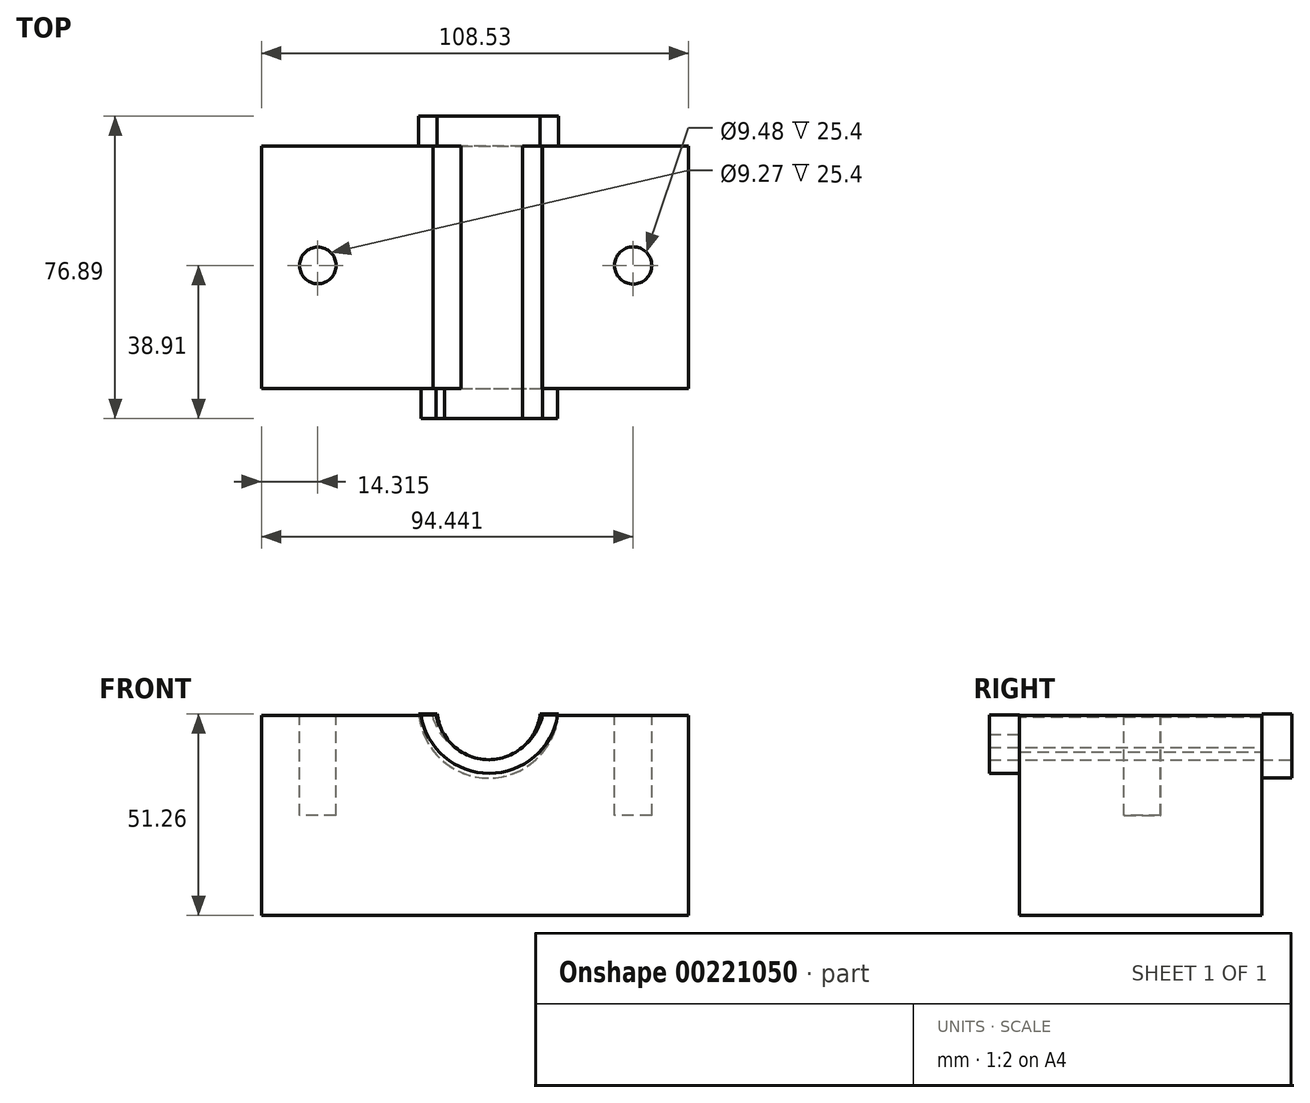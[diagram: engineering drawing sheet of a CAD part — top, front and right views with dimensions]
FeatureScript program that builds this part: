
annotation { "Feature Type Name" : "Feature", "Feature Type Description" : "" }
export const myFeature = defineFeature(function(context is Context, id is Id, definition is map)
    precondition{}
    {
        {
            var Q0;
            Q0=qCreatedBy(makeId("Top.planeOp"),FACE);
            var sketch = newSketch(context, id + "F0", { "sketchPlane" : qUnion([Q0])});
            skLineSegment(sketch, "E0.bottom", {"start": v(-43.41, 30.36) * mm, "end": v(65.12, 30.36) * mm});
            skLineSegment(sketch, "E0.top", {"start": v(-43.41, -31.29) * mm, "end": v(65.12, -31.29) * mm});
            skLineSegment(sketch, "E0.left", {"start": v(-43.41, 30.36) * mm, "end": v(-43.41, -31.29) * mm});
            skLineSegment(sketch, "E0.right", {"start": v(65.12, 30.36) * mm, "end": v(65.12, -31.29) * mm});
            skSolve(sketch);
        }
        {
            var Q0;
            Q0 = qSketchRegion(id + "F0", true);
            extrude(context, id + "F1", {"entities" : qUnion([Q0]), "depth" : 50.8 * mm});
        }
        {
            var Q0;
            Q0=makeQuery(id+"F1.opExtrude","CAP_FACE",FACE,{"disambiguationData":[OSD([sQuery(id+"F0.wireOp",EDGE,"E0.bottom"),sQuery(id+"F0.wireOp",EDGE,"E0.top"),sQuery(id+"F0.wireOp",EDGE,"E0.left"),sQuery(id+"F0.wireOp",EDGE,"E0.right")])],"isStart":false});
            var sketch = newSketch(context, id + "F2", { "sketchPlane" : qUnion([Q0])});
            skCircle(sketch, "E1", {"center": v(-29.1, 0) * mm, "radius": 4.64 * mm});
            skCircle(sketch, "E2", {"center": v(51.03, 0) * mm, "radius": 4.74 * mm});
            skSolve(sketch);
        }
        {
            var Q0;
            Q0 = qSketchRegion(id + "F2", true);
            extrude(context, id + "F3", {"entities" : qUnion([Q0]), "operationType" : NewBodyOperationType.REMOVE, "oppositeDirection" : true, "depth" : 25.4 * mm});
        }
        {
            var Q0;
            Q0=makeQuery(id+"F1.opExtrude","SWEPT_FACE",FACE,{"disambiguationData":[OSD([sQuery(id+"F0.wireOp",EDGE,"E0.top")])]});
            var sketch = newSketch(context, id + "F4", { "sketchPlane" : qUnion([Q0])});
            skArc(sketch, "E3", {"start": v(0, 50.8) * mm, "mid": v(13.74, 39.98) * mm, "end": v(27.48, 50.8) * mm});
            skSolve(sketch);
        }
        {
            var Q0;
            {var subQ3=sQuery(id+"F4.wireOp",EDGE,"E3");Q0=makeQuery(id+"F4.imprint","IMPRINT",FACE,{"disambiguationData":[TD([[makeQuery(id+"F4.imprint","IMPRINT",EDGE,{"derivedFrom":subQ3}),-1.0]])]});}
            var sketch = newSketch(context, id + "F5", { "sketchPlane" : qUnion([Q0])});
            skLineSegment(sketch, "E4", {"start": v(0, 50.7) * mm, "end": v(27.97, 50.7) * mm});
            skArc(sketch, "E5", {"start": v(0, 50.7) * mm, "mid": v(13.99, 39.99) * mm, "end": v(27.97, 50.7) * mm});
            skSolve(sketch);
        }
        {
            var Q0;
            Q0 = qSketchRegion(id + "F5", true);
            extrude(context, id + "F6", {"entities" : qUnion([Q0]), "operationType" : NewBodyOperationType.REMOVE, "oppositeDirection" : true, "depth" : 82.55 * mm});
        }
        {
            var Q0;
            {var subQ3=sQuery(id+"F4.wireOp",EDGE,"E3");Q0=makeQuery(id+"F4.imprint","IMPRINT",FACE,{"disambiguationData":[TD([[makeQuery(id+"F4.imprint","IMPRINT",EDGE,{"derivedFrom":subQ3}),-1.0]])]});}
            var sketch = newSketch(context, id + "F7", { "sketchPlane" : qUnion([Q0])});
            skCircle(sketch, "E6", {"center": v(14.32, 52.76) * mm, "radius": 13.13 * mm});
            skSolve(sketch);
        }
        {
            var Q0;
            Q0 = qSketchRegion(id + "F7", true);
            extrude(context, id + "F8", {"entities" : qUnion([Q0]), "operationType" : NewBodyOperationType.REMOVE, "oppositeDirection" : true, "depth" : 96.01 * mm});
        }
        {
            var Q0;
            {var subQ3=sQuery(id+"F4.wireOp",EDGE,"E3");Q0=makeQuery(id+"F4.imprint","IMPRINT",FACE,{"disambiguationData":[TD([[makeQuery(id+"F4.imprint","IMPRINT",EDGE,{"derivedFrom":subQ3}),-1.0]])]});}
            var sketch = newSketch(context, id + "F9", { "sketchPlane" : qUnion([Q0])});
            skLineSegment(sketch, "E7", {"start": v(-2.9, 50.93) * mm, "end": v(31.85, 50.93) * mm});
            skArc(sketch, "E8", {"start": v(-2.9, 50.93) * mm, "mid": v(14.47, 36.13) * mm, "end": v(31.85, 50.93) * mm});
            skSolve(sketch);
        }
        {
            var Q0;
            Q0 = qSketchRegion(id + "F9", true);
            extrude(context, id + "F10", {"entities" : qUnion([Q0]), "operationType" : NewBodyOperationType.ADD, "depth" : 7.62 * mm});
        }
        {
            var Q0;
            {var subQ3=sQuery(id+"F4.wireOp",EDGE,"E3");Q0=makeQuery(id+"F4.imprint","IMPRINT",FACE,{"disambiguationData":[TD([[makeQuery(id+"F4.imprint","IMPRINT",EDGE,{"derivedFrom":subQ3}),-1.0]])]});}
            var sketch = newSketch(context, id + "F11", { "sketchPlane" : qUnion([Q0])});
            skCircle(sketch, "E9", {"center": v(13.85, 54.61) * mm, "radius": 14.24 * mm});
            skSolve(sketch);
        }
        {
            var Q0;
            Q0 = qSketchRegion(id + "F11", true);
            extrude(context, id + "F12", {"entities" : qUnion([Q0]), "operationType" : NewBodyOperationType.REMOVE, "oppositeDirection" : true, "depth" : 91.7 * mm});
        }
        {
            var Q0;
            Q0=makeQuery(id+"F10.opExtrude","CAP_FACE",FACE,{"disambiguationData":[OSD([sQuery(id+"F9.wireOp",EDGE,"E7"),sQuery(id+"F9.wireOp",EDGE,"E8")])],"isStart":false});
            var sketch = newSketch(context, id + "F13", { "sketchPlane" : qUnion([Q0])});
            skCircle(sketch, "E10", {"center": v(14.47, 53.73) * mm, "radius": 13.82 * mm});
            skSolve(sketch);
        }
        {
            var Q0;
            Q0 = qSketchRegion(id + "F13", true);
            extrude(context, id + "F14", {"entities" : qUnion([Q0]), "operationType" : NewBodyOperationType.REMOVE, "oppositeDirection" : true, "depth" : 102.62 * mm});
        }
        {
            var Q0;
            Q0=makeQuery(id+"F1.opExtrude","SWEPT_FACE",FACE,{"disambiguationData":[OSD([sQuery(id+"F0.wireOp",EDGE,"E0.bottom")])]});
            var sketch = newSketch(context, id + "F15", { "sketchPlane" : qUnion([Q0])});
            skCircle(sketch, "E11", {"center": v(-14.32, 52.76) * mm, "radius": 17.83 * mm});
            skSolve(sketch);
        }
        {
            var Q0;
            Q0 = qSketchRegion(id + "F15", true);
            extrude(context, id + "F16", {"entities" : qUnion([Q0]), "operationType" : NewBodyOperationType.ADD, "depth" : 7.62 * mm});
        }
        {
            var Q0;
            Q0=makeQuery(id+"F16.opExtrude","CAP_FACE",FACE,{"disambiguationData":[OSD([sQuery(id+"F15.wireOp",EDGE,"E11")])],"isStart":false});
            var sketch = newSketch(context, id + "F17", { "sketchPlane" : qUnion([Q0])});
            skCircle(sketch, "E12", {"center": v(-14.32, 52.76) * mm, "radius": 13.16 * mm});
            skSolve(sketch);
        }
        {
            var Q0;
            Q0 = qSketchRegion(id + "F17", true);
            extrude(context, id + "F18", {"entities" : qUnion([Q0]), "operationType" : NewBodyOperationType.REMOVE, "oppositeDirection" : true, "depth" : 136.14 * mm});
        }
        {
            var Q0;
            Q0=makeQuery(id+"F16.opExtrude","CAP_FACE",FACE,{"disambiguationData":[OSD([sQuery(id+"F15.wireOp",EDGE,"E11")])],"isStart":false});
            var sketch = newSketch(context, id + "F19", { "sketchPlane" : qUnion([Q0])});
            skLineSegment(sketch, "E13.bottom", {"start": v(-32.92, 51.26) * mm, "end": v(17.88, 51.26) * mm});
            skLineSegment(sketch, "E13.top", {"start": v(-32.92, 75.97) * mm, "end": v(17.88, 75.97) * mm});
            skLineSegment(sketch, "E13.left", {"start": v(-32.92, 51.26) * mm, "end": v(-32.92, 75.97) * mm});
            skLineSegment(sketch, "E13.right", {"start": v(17.88, 51.26) * mm, "end": v(17.88, 75.97) * mm});
            skSolve(sketch);
        }
        {
            var Q0;
            Q0 = qSketchRegion(id + "F19", true);
            extrude(context, id + "F20", {"entities" : qUnion([Q0]), "operationType" : NewBodyOperationType.REMOVE, "oppositeDirection" : true, "depth" : 25.4 * mm});
        }
    });
